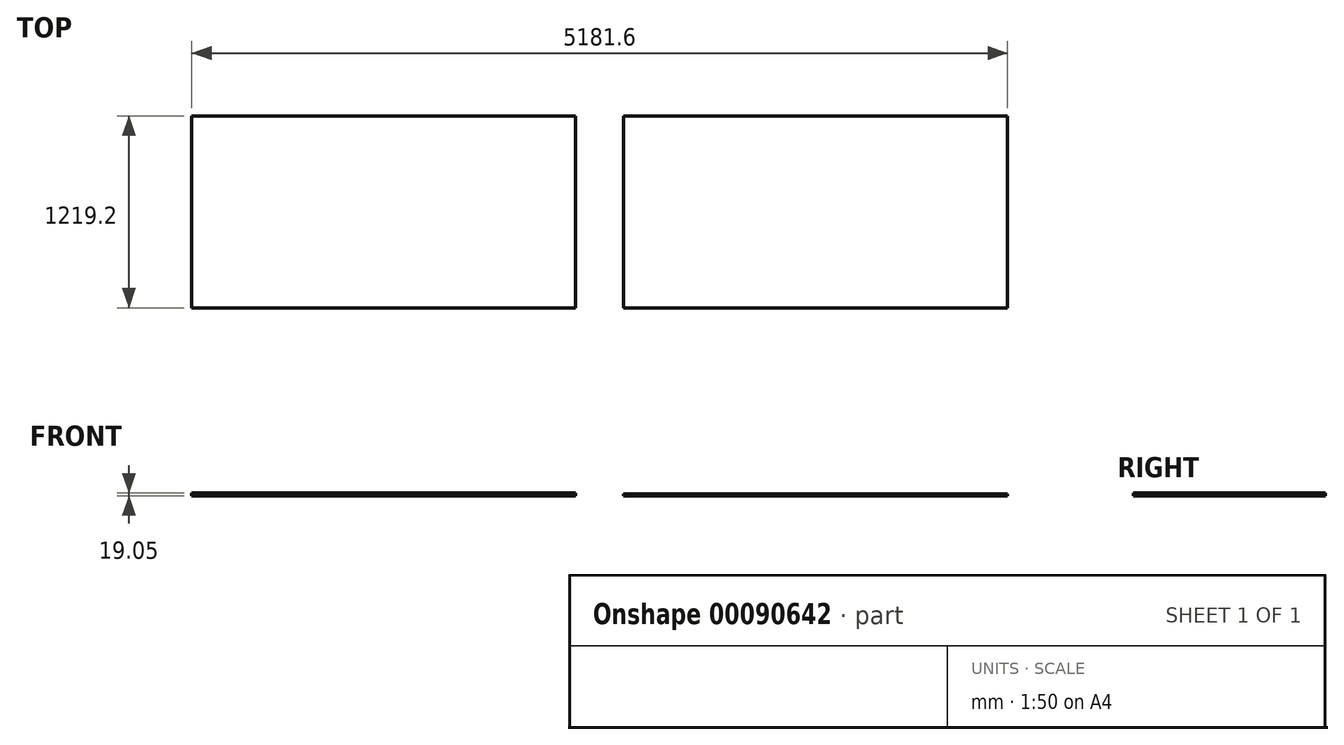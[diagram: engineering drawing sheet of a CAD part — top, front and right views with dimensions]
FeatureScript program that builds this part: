
annotation { "Feature Type Name" : "Feature", "Feature Type Description" : "" }
export const myFeature = defineFeature(function(context is Context, id is Id, definition is map)
    precondition{}
    {
        {
            var Q0;
            Q0=qCreatedBy(makeId("Top.planeOp"),FACE);
            var sketch = newSketch(context, id + "F0", { "sketchPlane" : qUnion([Q0])});
            skLineSegment(sketch, "E0.bottom", {"start": v(-304.8, 609.6) * mm, "end": v(-2743.2, 609.6) * mm});
            skLineSegment(sketch, "E0.top", {"start": v(-304.8, -609.6) * mm, "end": v(-2743.2, -609.6) * mm});
            skLineSegment(sketch, "E0.left", {"start": v(-304.8, 609.6) * mm, "end": v(-304.8, -609.6) * mm});
            skLineSegment(sketch, "E0.right", {"start": v(-2743.2, 609.6) * mm, "end": v(-2743.2, -609.6) * mm});
            skPoint(sketch, "E0.middle", {"position": v(-1524, 0) * mm});
            skLineSegment(sketch, "E1.bottom", {"start": v(0, 609.6) * mm, "end": v(2438.4, 609.6) * mm});
            skLineSegment(sketch, "E1.top", {"start": v(0, -609.6) * mm, "end": v(2438.4, -609.6) * mm});
            skLineSegment(sketch, "E1.left", {"start": v(0, 609.6) * mm, "end": v(0, -609.6) * mm});
            skLineSegment(sketch, "E1.right", {"start": v(2438.4, 609.6) * mm, "end": v(2438.4, -609.6) * mm});
            skSolve(sketch);
        }
        {
            var Q0;
            Q0=makeQuery(id+"F0.imprint","IMPRINT",FACE,{"disambiguationData":[TD([[makeQuery(id+"F0.imprint","IMPRINT",EDGE,{"derivedFrom":sQuery(id+"F0.wireOp",EDGE,"E0.bottom")}),1.0]])]});
            extrude(context, id + "F1", {"entities" : qUnion([Q0]), "depth" : 19.05 * mm});
        }
        {
            var Q0;
            Q0=makeQuery(id+"F0.imprint","IMPRINT",FACE,{"disambiguationData":[TD([[makeQuery(id+"F0.imprint","IMPRINT",EDGE,{"derivedFrom":sQuery(id+"F0.wireOp",EDGE,"E1.bottom")}),-1.0]])]});
            extrude(context, id + "F2", {"entities" : qUnion([Q0]), "depth" : 12.7 * mm});
        }
    });
